# Revit family: BE_84174_de_DE
name_source: partatom
category: Leuchten
units: mm (PartAtom-declared; Revit-internal decimal feet)

## family parameters
Basisbauteil = Fläche
Beim Laden mit Abzugskörper schneiden = Ja
Bemaßung runder Anschluss = Durchmesser verwenden
Gemeinsam genutzt = Nein
Lichtquelle = Ja
Raumberechnungspunkt = Ja
Teiletyp = Normal

## types (2) — shared parameters
AC/DC = AC/DC
Aktualisierung = 2022-05-19T04:00:07
Anschlussleitung = 1.8 m 07RN8-F 5 G 1²
BEGA_Dummy = Nein
BEGA_IES = Ja
BEGA_Intern = Ja
BEGA_Intern_Konstruktion = Ja
BEGA_Intern_an = Ja
BEGA_Intern_aus = Ja
Befestigungsabstand = 170 x 170 mm
Befestigungsbohrung = Ø 9 mm
Beschreibung = Bodenaufbauscheinwerfer
Beschreibung_Sonderanfertigung = Hier können Sie Informationen zur Sonderanfertigung eintragen.
Bestellnummer_Einbaugehäuse = ---
Bestellnummer_Erdstück = ---
CE_Konformität = ja
ENEC = ja
Einbaugehäuse = Nein
Energieeffizienzklasse = LED A++ - A
Erdstück = Nein
Farbfilter = 16777215
Farbtemperaturverschiebung bei Dämpfen der Lampe = <Keine Auswahl>
Farbwiedergabeindex = CRI > 80
Frequenz = 0/50-60 Hz
Gewicht = 5.2 kg
Hersteller = BEGA
Lampe = LED 29.1 W
Lastklassifizierung = Beleuchtung
Lebensdauerkriterien = L70B50 @ 25 °C = 200000 h
Logo = BEGA_Logo.png
M_A = Nein
M_G = Ja
M_W = Nein
Material_02 = BEGA_Oberfläche_Silber_matt
Material_03 = BEGA_Oberfläche_Weiss_matt
Material_06 = BEGA_Oberfläche_Edelstahl_gebürstet
Material_09 = BEGA_Glas_klar
Material_10 = BEGA_Glas_matt
Material_11 = BEGA_Glas_opal
Material_15 = BEGA_Leuchtmedium_matt
Material_17 = BEGA_Reflektor
Neigungswinkel = 0.00°
Oberflächentemperatur = 30 °C
Produktdatenblatt = https://cdn.bega.com
Scheinlast = 0 VA
Schutzart = IP 67
Schutzklasse = I
Sonderanfertigung = Nein
Spannung = 240 V
Typenbild = 84174.png
URL = https://www.bega.com
Umgebungstemperatur = 25 °C
zero-valued in all types: Vorgabe-Ansicht

## per-type parameters (varying)
| type | Bestellnummer | Datei für fotometrisches Netz | Farbtemperatur | LED_Modulbezeichnung | Lampenlichtstrom | Leuchtenlichtstrom | Modell |
| BEGA_84174_Grafit_K3 | 84174K3 | BE_84174K3.IES | 3000 K | LED-0903/830 | 5640 lm | 4085 lm | 84174K3 |
| BEGA_84174_Grafit_K4 | 84174K4 | BE_84174K4.IES | 4000 K | LED-0903/840 | 5800 lm | 4201 lm | 84174K4 |
